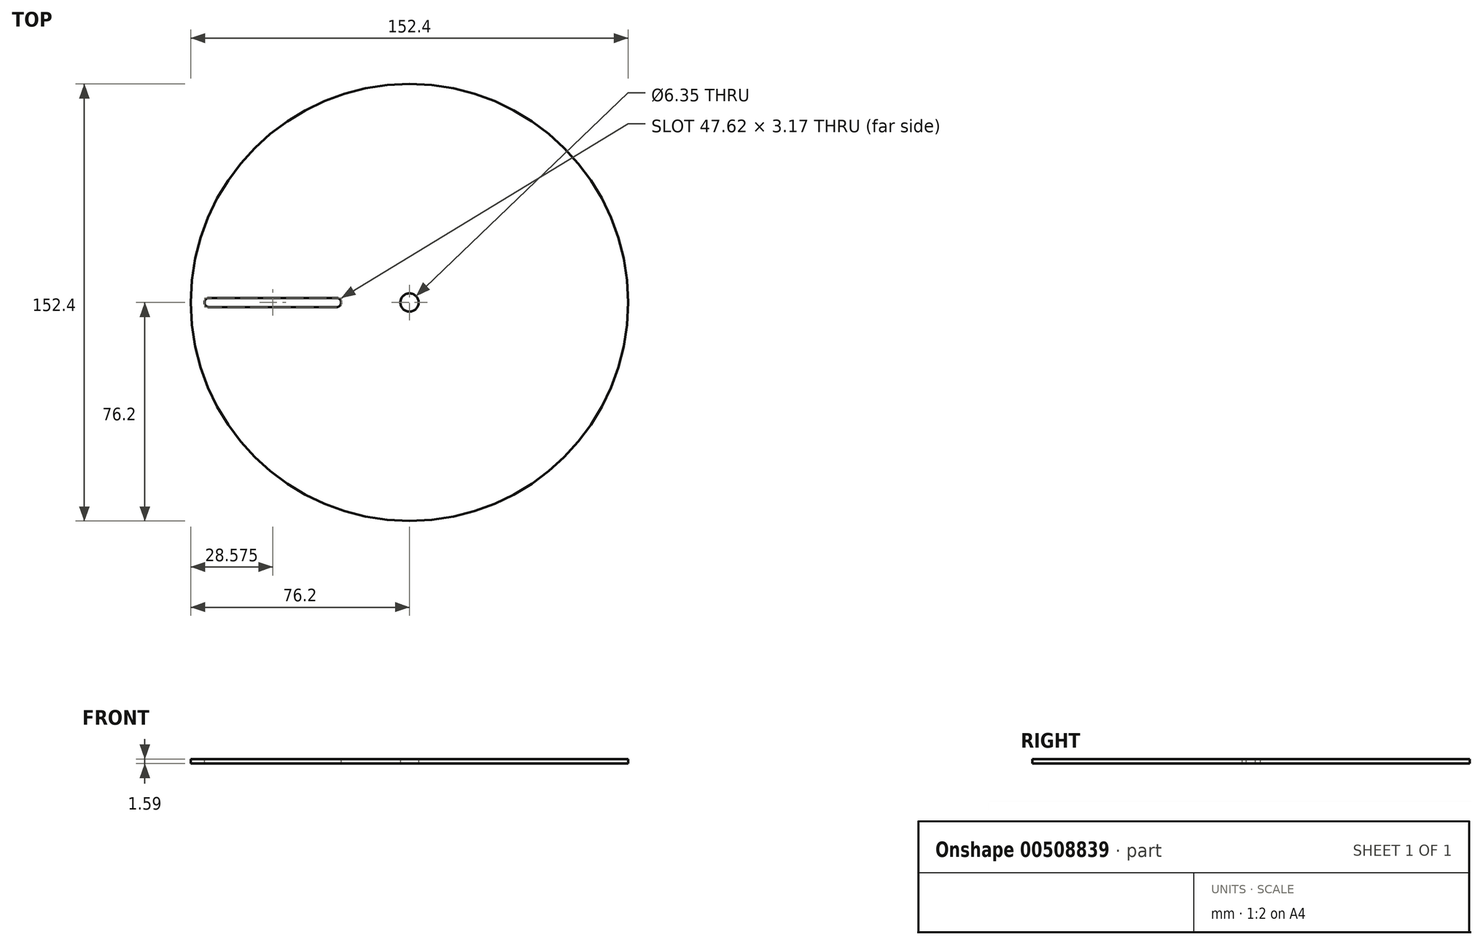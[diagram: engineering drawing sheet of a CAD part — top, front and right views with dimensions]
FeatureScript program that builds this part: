
annotation { "Feature Type Name" : "Feature", "Feature Type Description" : "" }
export const myFeature = defineFeature(function(context is Context, id is Id, definition is map)
    precondition{}
    {
        {
            var Q0;
            Q0=qCreatedBy(makeId("Top.planeOp"),FACE);
            var sketch = newSketch(context, id + "F0", { "sketchPlane" : qUnion([Q0])});
            skCircle(sketch, "E0", {"center": v(0, 0) * mm, "radius": 76.2 * mm});
            skCircle(sketch, "E1", {"center": v(0, 0) * mm, "radius": 3.18 * mm});
            skSolve(sketch);
        }
        {
            var Q0;
            Q0=makeQuery(id+"F0.imprint","IMPRINT",FACE,{"disambiguationData":[TD([[makeQuery(id+"F0.imprint","IMPRINT",EDGE,{"derivedFrom":sQuery(id+"F0.wireOp",EDGE,"E0")}),1.0]])]});
            extrude(context, id + "F1", {"entities" : qUnion([Q0]), "depth" : 1.59 * mm});
        }
        {
            var Q0;
            Q0=makeQuery(id+"F1.opExtrude","CAP_FACE",FACE,{"disambiguationData":[OSD([sQuery(id+"F0.wireOp",EDGE,"E0"),sQuery(id+"F0.wireOp",EDGE,"E1")])],"isStart":false});
            var sketch = newSketch(context, id + "F2", { "sketchPlane" : qUnion([Q0])});
            skArc(sketch, "E2", {"start": v(-69.85, 1.59) * mm, "mid": v(-71.44, 0) * mm, "end": v(-69.85, -1.59) * mm});
            skArc(sketch, "E3", {"start": v(-25.4, -1.59) * mm, "mid": v(-23.81, 0) * mm, "end": v(-25.4, 1.59) * mm});
            skLineSegment(sketch, "E4", {"start": v(-69.85, -1.59) * mm, "end": v(-25.4, -1.59) * mm});
            skLineSegment(sketch, "E5", {"start": v(-69.85, 1.59) * mm, "end": v(-25.4, 1.59) * mm});
            skSolve(sketch);
        }
        {
            var Q0;
            Q0=makeQuery(id+"F2.imprint","IMPRINT",FACE,{"disambiguationData":[TD([[makeQuery(id+"F2.imprint","IMPRINT",EDGE,{"derivedFrom":sQuery(id+"F2.wireOp",EDGE,"E2")}),1.0]])]});
            extrude(context, id + "F3", {"entities" : qUnion([Q0]), "operationType" : NewBodyOperationType.REMOVE, "oppositeDirection" : true, "depth" : 25.4 * mm});
        }
    });
